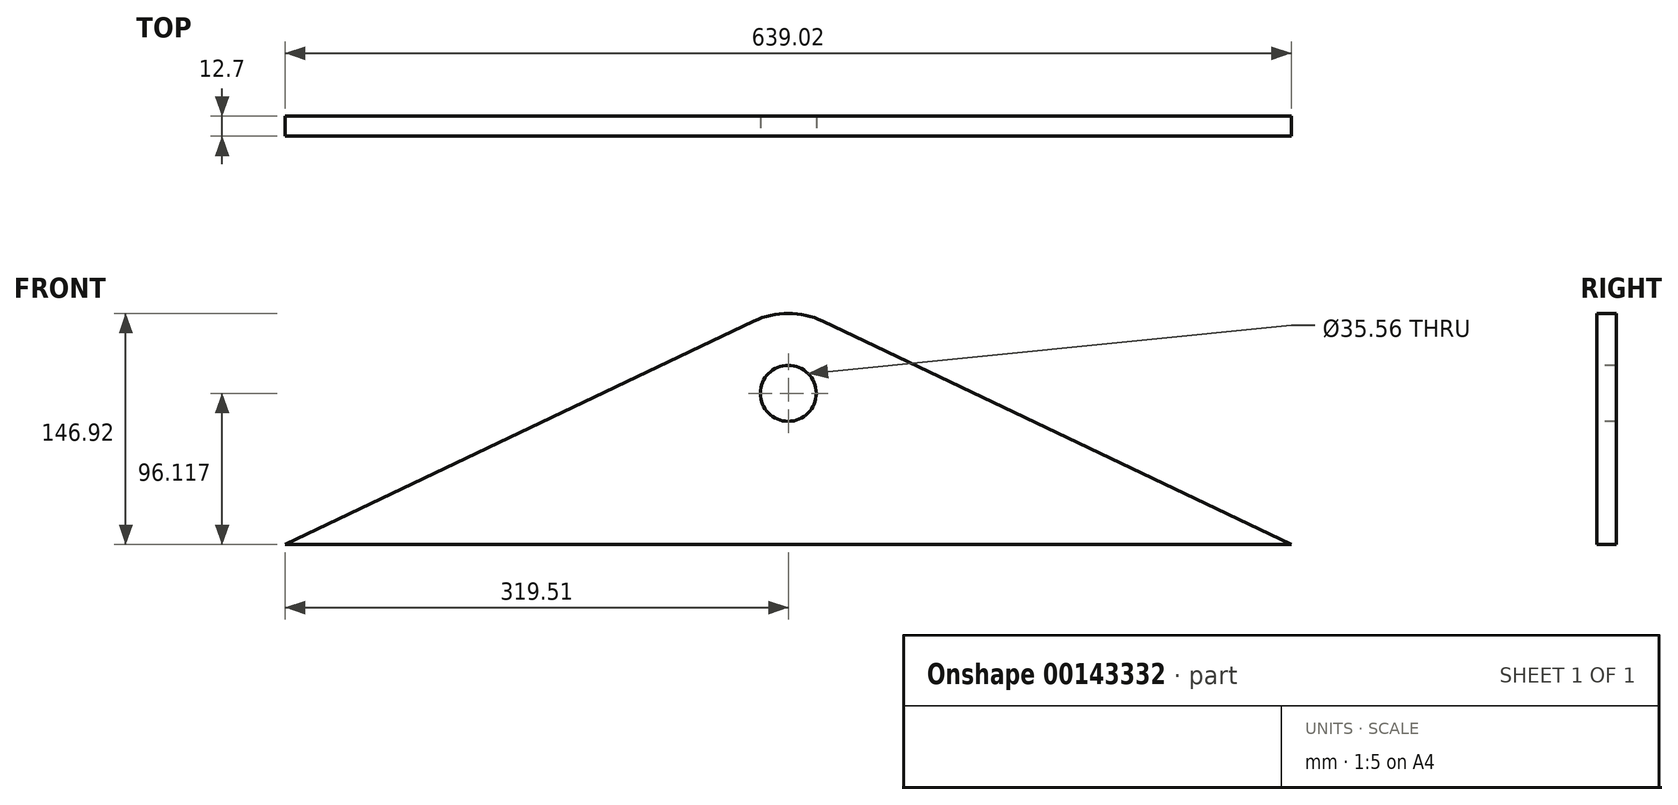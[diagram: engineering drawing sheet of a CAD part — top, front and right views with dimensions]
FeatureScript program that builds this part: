
annotation { "Feature Type Name" : "Feature", "Feature Type Description" : "" }
export const myFeature = defineFeature(function(context is Context, id is Id, definition is map)
    precondition{}
    {
        {
            var Q0;
            Q0=qCreatedBy(makeId("Front.planeOp"),FACE);
            var sketch = newSketch(context, id + "F0", { "sketchPlane" : qUnion([Q0])});
            skLineSegment(sketch, "E0", {"start": v(-319.51, 0) * mm, "end": v(319.51, 0) * mm});
            skLineSegment(sketch, "E1", {"start": v(319.51, 0) * mm, "end": v(21.87, 141.97) * mm});
            skLineSegment(sketch, "E2", {"start": v(-21.87, 141.97) * mm, "end": v(-319.51, 0) * mm});
            skLineSegment(sketch, "E3", {"start": v(0, 0) * mm, "end": v(0, 484.08) * mm, "construction": true});
            skPoint(sketch, "E4.visualSharp", {"position": v(0, 152.4) * mm});
            skArc(sketch, "E4.filletArc", {"start": v(21.87, 141.97) * mm, "mid": v(0, 146.92) * mm, "end": v(-21.87, 141.97) * mm});
            skSolve(sketch);
        }
        {
            var Q0;
            Q0 = qSketchRegion(id + "F0", true);
            extrude(context, id + "F1", {"entities" : qUnion([Q0]), "depth" : 12.7 * mm});
        }
        {
            var Q0;
            Q0=makeQuery(id+"F1.opExtrude","CAP_FACE",FACE,{"disambiguationData":[OSD([sQuery(id+"F0.wireOp",EDGE,"E0"),sQuery(id+"F0.wireOp",EDGE,"E1"),sQuery(id+"F0.wireOp",EDGE,"E2"),sQuery(id+"F0.wireOp",EDGE,"E4.filletArc")])],"isStart":false});
            var sketch = newSketch(context, id + "F2", { "sketchPlane" : qUnion([Q0])});
            skLineSegment(sketch, "E5", {"start": v(0, 0) * mm, "end": v(0, 146.92) * mm, "construction": true});
            skArc(sketch, "E6.0", {"start": v(21.87, 141.97) * mm, "mid": v(0, 146.92) * mm, "end": v(-21.87, 141.97) * mm, "construction": true});
            skCircle(sketch, "E7", {"center": v(0, 96.12) * mm, "radius": 17.78 * mm});
            skSolve(sketch);
        }
        {
            var Q0;
            Q0 = qSketchRegion(id + "F2", true);
            extrude(context, id + "F3", {"entities" : qUnion([Q0]), "operationType" : NewBodyOperationType.REMOVE, "endBound" : BoundingType.THROUGH_ALL, "oppositeDirection" : true, "depth" : 25.4 * mm});
        }
    });
